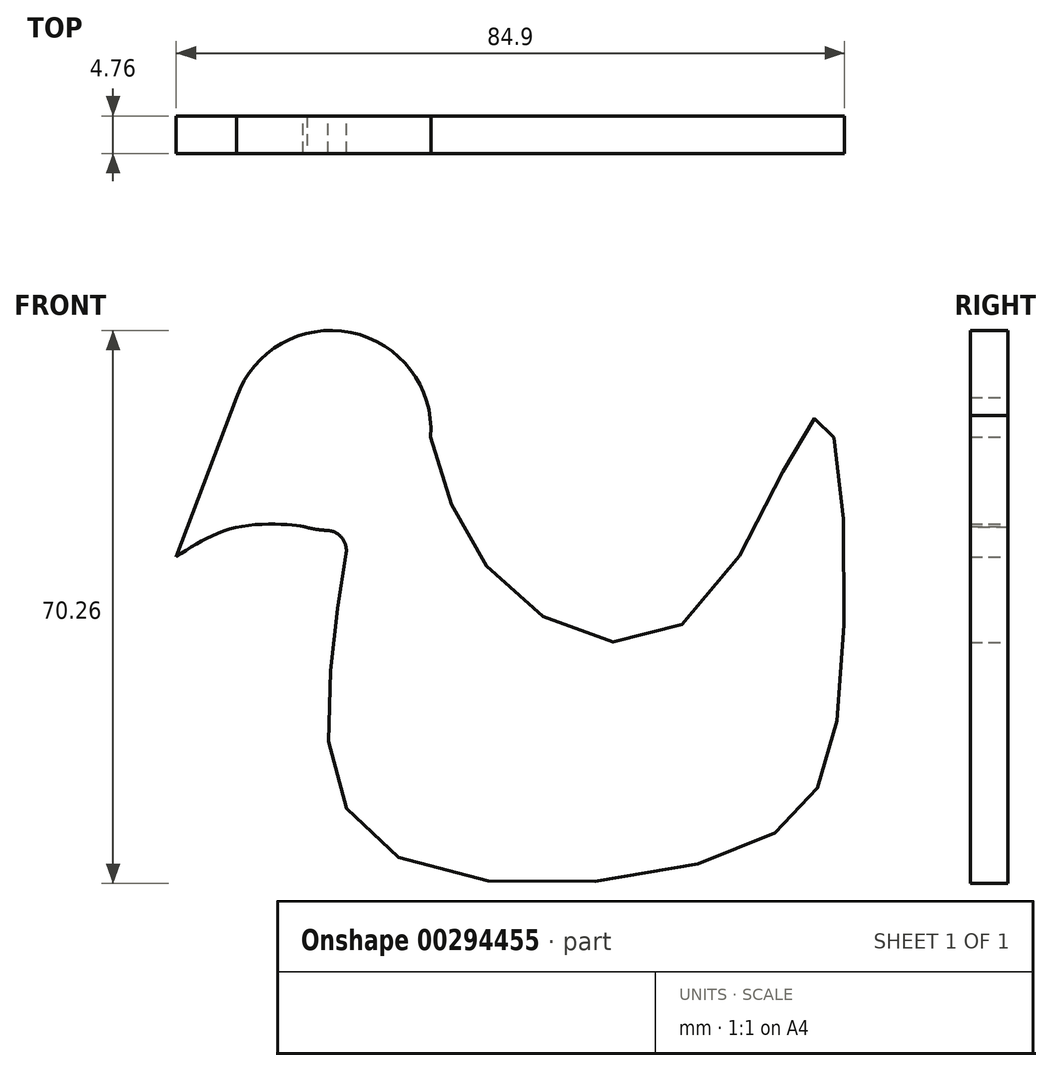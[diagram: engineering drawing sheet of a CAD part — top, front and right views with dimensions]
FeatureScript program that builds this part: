
annotation { "Feature Type Name" : "Feature", "Feature Type Description" : "" }
export const myFeature = defineFeature(function(context is Context, id is Id, definition is map)
    precondition{}
    {
        {
            var Q0;
            Q0=qCreatedBy(makeId("Front.planeOp"),FACE);
            var sketch = newSketch(context, id + "F0", { "sketchPlane" : qUnion([Q0])});
            skCircle(sketch, "E0", {"center": v(0, 0) * mm, "radius": 12.7 * mm});
            skLineSegment(sketch, "E1", {"start": v(-11.99, 4.2) * mm, "end": v(-19.66, -16.04) * mm});
            skFitSpline(sketch, "E2", {"points": [v(11.31, 5.77) * mm, v(20.9, -18.58) * mm, v(44.87, -24.47) * mm, v(62.13, 1.88) * mm, v(64.71, -32.53) * mm, v(53.4, -52.73) * mm, v(6.04, -52.73) * mm, v(0, -29.78) * mm, v(2.47, -12.46) * mm], "startDerivative": vector(42.19, -217.05) * mm, "endDerivative": vector(27.7, 160.37) * mm});
            skFitSpline(sketch, "E3", {"points": [v(-19.66, -16.04) * mm, v(-11.33, -12.17) * mm, v(-3.54, -12.2) * mm, v(-3.03, -12.33) * mm], "startDerivative": vector(16.36, 10.62) * mm, "endDerivative": vector(3.02, -1.13) * mm});
            skSolve(sketch);
        }
        {
            var Q0;
            Q0=makeQuery(id+"F0.imprint","IMPRINT",FACE,{"disambiguationData":[TD([[makeQuery(id+"F0.imprint","IMPRINT",EDGE,{"derivedFrom":sQuery(id+"F0.wireOp",EDGE,"E0")}),1.0]])]});
            var Q1;
            {var subQ0=sQuery(id+"F0.wireOp",EDGE,"E1");Q1=makeQuery(id+"F0.imprint","IMPRINT",FACE,{"disambiguationData":[TD([[makeQuery(id+"F0.imprint","IMPRINT",EDGE,{"derivedFrom":subQ0}),1.0]])]});}
            var Q2;
            {var subQ0=sQuery(id+"F0.wireOp",EDGE,"E2");var subQ1=sQuery(id+"F0.wireOp",EDGE,"E0");var subQ3=makeQuery(id+"F0.imprint","INTERSECT",VERTEX,{"disambiguationData":[OD(1.0)],"derivedFrom":[subQ1,subQ0]});Q2=makeQuery(id+"F0.imprint","IMPRINT",FACE,{"disambiguationData":[TD([[makeQuery(id+"F0.imprint","IMPRINT",EDGE,{"disambiguationData":[TD([[subQ3,1.0]])],"derivedFrom":subQ1}),-1.0]])]});}
            var Q3;
            {var subQ0=sQuery(id+"F0.wireOp",EDGE,"E2");var subQ1=sQuery(id+"F0.wireOp",EDGE,"E0");var subQ2=makeQuery(id+"F0.imprint","INTERSECT",VERTEX,{"disambiguationData":[OD(0.0)],"derivedFrom":[subQ1,subQ0]});Q3=makeQuery(id+"F0.imprint","IMPRINT",FACE,{"disambiguationData":[TD([[makeQuery(id+"F0.imprint","IMPRINT",EDGE,{"disambiguationData":[TD([[subQ2,1.0]])],"derivedFrom":subQ1}),1.0]])]});}
            var Q4;
            {var subQ0=sQuery(id+"F0.wireOp",EDGE,"E2");var subQ1=sQuery(id+"F0.wireOp",EDGE,"E0");var subQ2=makeQuery(id+"F0.imprint","INTERSECT",VERTEX,{"disambiguationData":[OD(1.0)],"derivedFrom":[subQ1,subQ0]});Q4=makeQuery(id+"F0.imprint","IMPRINT",FACE,{"disambiguationData":[TD([[makeQuery(id+"F0.imprint","IMPRINT",EDGE,{"disambiguationData":[TD([[subQ2,-1.0]])],"derivedFrom":subQ1}),-1.0]])]});}
            extrude(context, id + "F1", {"entities" : qUnion([Q0, Q1, Q2, Q3, Q4]), "depth" : 4.76 * mm});
        }
        {
            var Q0;
            {var subQ0=sQuery(id+"F0.wireOp",EDGE,"E2");var subQ1=sQuery(id+"F0.wireOp",EDGE,"E0");Q0=makeQuery(id+"F1.opExtrude","SWEPT_EDGE",EDGE,{"disambiguationData":[OSD([subQ1,subQ0]),TDD([makeQuery(id+"F0.imprint","INTERSECT",VERTEX,{"disambiguationData":[OD(1.0)],"derivedFrom":[subQ1,subQ0]})])]});}
            fillet(context, id + "F2", {"entities" : qUnion([Q0]), "radius" : 2.54 * mm, "tangentPropagation" : true, "allowEdgeOverflow" : false});
        }
    });
